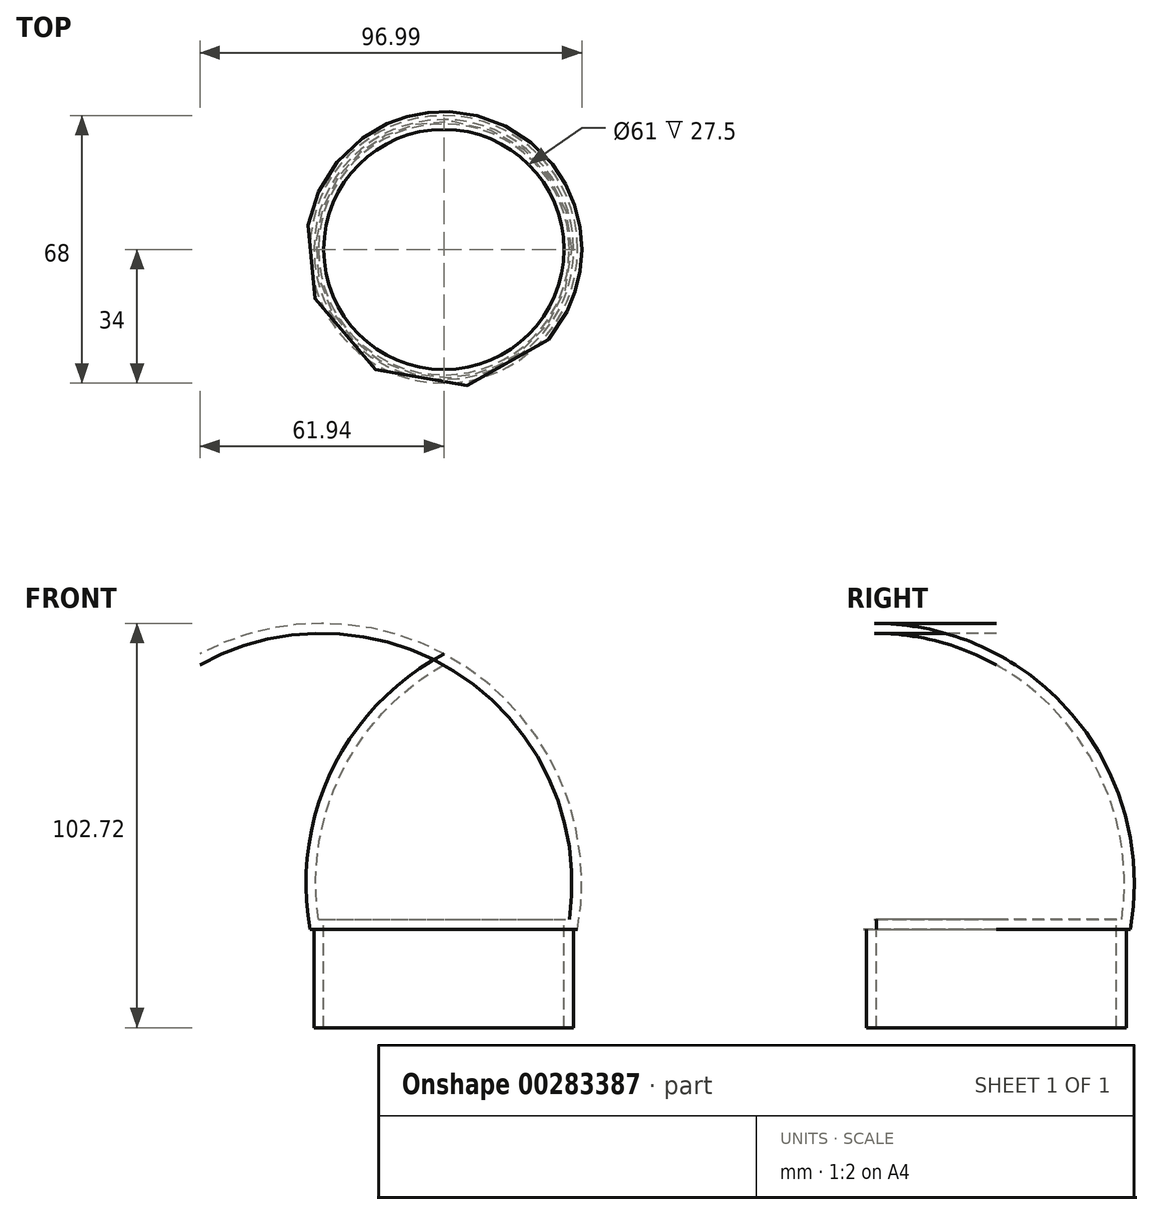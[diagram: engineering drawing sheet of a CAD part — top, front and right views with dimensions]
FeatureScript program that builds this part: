
annotation { "Feature Type Name" : "Feature", "Feature Type Description" : "" }
export const myFeature = defineFeature(function(context is Context, id is Id, definition is map)
    precondition{}
    {
        {
            var Q0;
            Q0=qCreatedBy(makeId("Front.planeOp"),FACE);
            var sketch = newSketch(context, id + "F0", { "sketchPlane" : qUnion([Q0])});
            skLineSegment(sketch, "E0", {"start": v(0, 27.64) * mm, "end": v(34, 27.64) * mm});
            skLineSegment(sketch, "E1", {"start": v(0, 27.64) * mm, "end": v(0, 97.64) * mm});
            skLineSegment(sketch, "E2", {"start": v(0, 20.97) * mm, "end": v(0, 112.46) * mm});
            skArc(sketch, "E3", {"start": v(34, 27.64) * mm, "mid": v(28.41, 68.18) * mm, "end": v(0, 97.64) * mm});
            skSolve(sketch);
        }
        {
            var Q0;
            {var subQ0=sQuery(id+"F0.wireOp",EDGE,"E0");Q0=makeQuery(id+"F0.imprint","IMPRINT",FACE,{"disambiguationData":[TD([[makeQuery(id+"F0.imprint","IMPRINT",EDGE,{"derivedFrom":subQ0}),1.0]])]});}
            var Q1;
            Q1=sQuery(id+"F0.wireOp",EDGE,"E2");
            revolve(context, id + "F1", {"entities" : qUnion([Q0]), "axis" : qUnion([Q1]), "revolveType" : RevolveType.FULL});
        }
        {
            var Q0;
            Q0=makeQuery(id+"F1.opRevolve","SWEPT_FACE",FACE,{"disambiguationData":[OSD([sQuery(id+"F0.wireOp",EDGE,"E0")])]});
            var sketch = newSketch(context, id + "F2", { "sketchPlane" : qUnion([Q0])});
            skCircle(sketch, "E4", {"center": v(0, 0) * mm, "radius": 33 * mm});
            skSolve(sketch);
        }
        {
            var Q0;
            Q0=makeQuery(id+"F2.imprint","IMPRINT",FACE,{"disambiguationData":[TD([[makeQuery(id+"F2.imprint","IMPRINT",EDGE,{"derivedFrom":sQuery(id+"F2.wireOp",EDGE,"E4")}),1.0]])]});
            extrude(context, id + "F3", {"entities" : qUnion([Q0]), "operationType" : NewBodyOperationType.ADD, "depth" : 25 * mm});
        }
        {
            var Q0;
            Q0=makeQuery(id+"F3.opExtrude","CAP_FACE",FACE,{"disambiguationData":[OSD([sQuery(id+"F2.wireOp",EDGE,"E4")])],"isStart":false});
            shell(context, id + "F4", {"entities" : qUnion([Q0]), "thickness" : 2.5 * mm});
        }
    });
